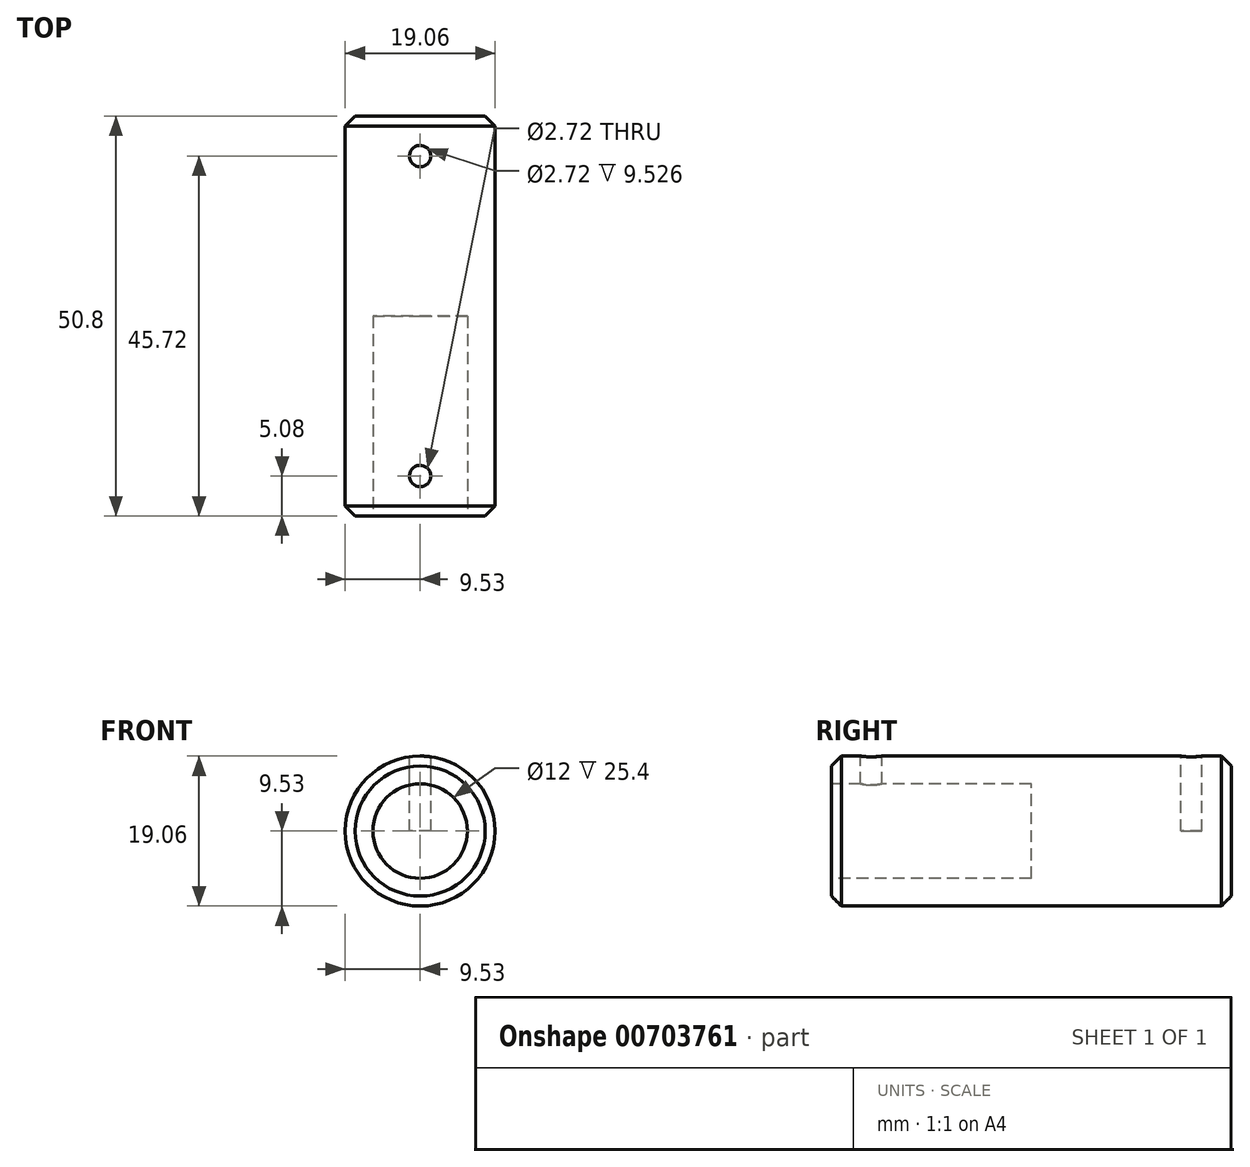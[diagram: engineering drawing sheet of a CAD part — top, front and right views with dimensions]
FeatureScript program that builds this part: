
annotation { "Feature Type Name" : "Feature", "Feature Type Description" : "" }
export const myFeature = defineFeature(function(context is Context, id is Id, definition is map)
    precondition{}
    {
        {
            var Q0;
            Q0=qCreatedBy(makeId("Front.planeOp"),FACE);
            var sketch = newSketch(context, id + "F0", { "sketchPlane" : qUnion([Q0])});
            skCircle(sketch, "E0", {"center": v(0, 0) * mm, "radius": 9.53 * mm});
            skSolve(sketch);
        }
        {
            var Q0;
            Q0=makeQuery(id+"F0.imprint","IMPRINT",FACE,{"disambiguationData":[TD([[makeQuery(id+"F0.imprint","IMPRINT",EDGE,{"derivedFrom":sQuery(id+"F0.wireOp",EDGE,"E0")}),1.0]])]});
            extrude(context, id + "F1", {"entities" : qUnion([Q0]), "depth" : 25.4 * mm, "offsetDistance" : 25.4 * mm, "hasSecondDirection" : true, "secondDirectionOppositeDirection" : true, "secondDirectionDepth" : 25.4 * mm});
        }
        {
            var Q0;
            Q0=qCreatedBy(makeId("Front.planeOp"),FACE);
            var sketch = newSketch(context, id + "F2", { "sketchPlane" : qUnion([Q0])});
            skPoint(sketch, "E1", {"position": v(0, 0) * mm});
            skSolve(sketch);
        }
        {
            var Q0;
            Q0=sQuery(id+"F2.wireOp",VERTEX,"E1");
            var Q1;
            Q1=makeQuery(id+"F1.opExtrude","SWEPT_BODY",BODY,{"disambiguationData":[OSD([sQuery(id+"F0.wireOp",EDGE,"E0")])]});
            hole(context, id + "F3", {"style" : HoleStyle.SIMPLE, "endStyle" : HoleEndStyle.THROUGH, "oppositeDirection" : true, "holeDiameter" : 12 * mm, "majorDiameter" : 6.35 * mm, "isTappedThrough" : true, "tappedDepth" : 12.7 * mm, "tapClearance" : 3, "locations" : qUnion([Q0]), "scope" : qUnion([Q1]), "startStyle" : HoleStartStyle.PART});
        }
        {
            var Q0;
            Q0=makeQuery(id+"F1.opExtrude","CAP_EDGE",EDGE,{"disambiguationData":[OSD([sQuery(id+"F0.wireOp",EDGE,"E0")])],"isStart":false});
            var Q1;
            Q1=makeQuery(id+"F1.opExtrude","CAP_EDGE",EDGE,{"disambiguationData":[OSD([sQuery(id+"F0.wireOp",EDGE,"E0")])],"isStart":true});
            chamfer(context, id + "F4", {"entities" : qUnion([Q0, Q1]), "width" : 1.27 * mm, "tangentPropagation" : true});
        }
        {
            var Q0;
            Q0=qCreatedBy(makeId("Top.planeOp"),FACE);
            var sketch = newSketch(context, id + "F5", { "sketchPlane" : qUnion([Q0])});
            skPoint(sketch, "E2", {"position": v(0, 3.2) * mm});
            skLineSegment(sketch, "E3", {"start": v(-18.8, 0) * mm, "end": v(18.12, 0) * mm, "construction": true});
            skPoint(sketch, "E4.startSnap0", {"position": v(-0.33, 0) * mm});
            skPoint(sketch, "E5", {"position": v(0, 20.32) * mm});
            skPoint(sketch, "E6.MirrorP", {"position": v(0, -20.32) * mm});
            skLineSegment(sketch, "E7", {"start": v(0, 3.2) * mm, "end": v(0, 25.4) * mm, "construction": true});
            skLineSegment(sketch, "E8", {"start": v(0, 3.2) * mm, "end": v(0, -25.4) * mm, "construction": true});
            skSolve(sketch);
        }
        {
            var Q0;
            Q0=sQuery(id+"F5.wireOp",VERTEX,"E5");
            var Q1;
            Q1=sQuery(id+"F5.wireOp",VERTEX,"E6.MirrorP");
            var Q2;
            Q2=makeQuery(id+"F1.opExtrude","SWEPT_BODY",BODY,{"disambiguationData":[OSD([sQuery(id+"F0.wireOp",EDGE,"E0")])]});
            hole(context, id + "F6", {"style" : HoleStyle.SIMPLE, "endStyle" : HoleEndStyle.THROUGH, "oppositeDirection" : true, "holeDiameter" : 2.72 * mm, "majorDiameter" : 6.35 * mm, "isTappedThrough" : true, "tappedDepth" : 12.7 * mm, "tapClearance" : 3, "locations" : qUnion([Q0, Q1]), "scope" : qUnion([Q2]), "startStyle" : HoleStartStyle.PART});
        }
    });
